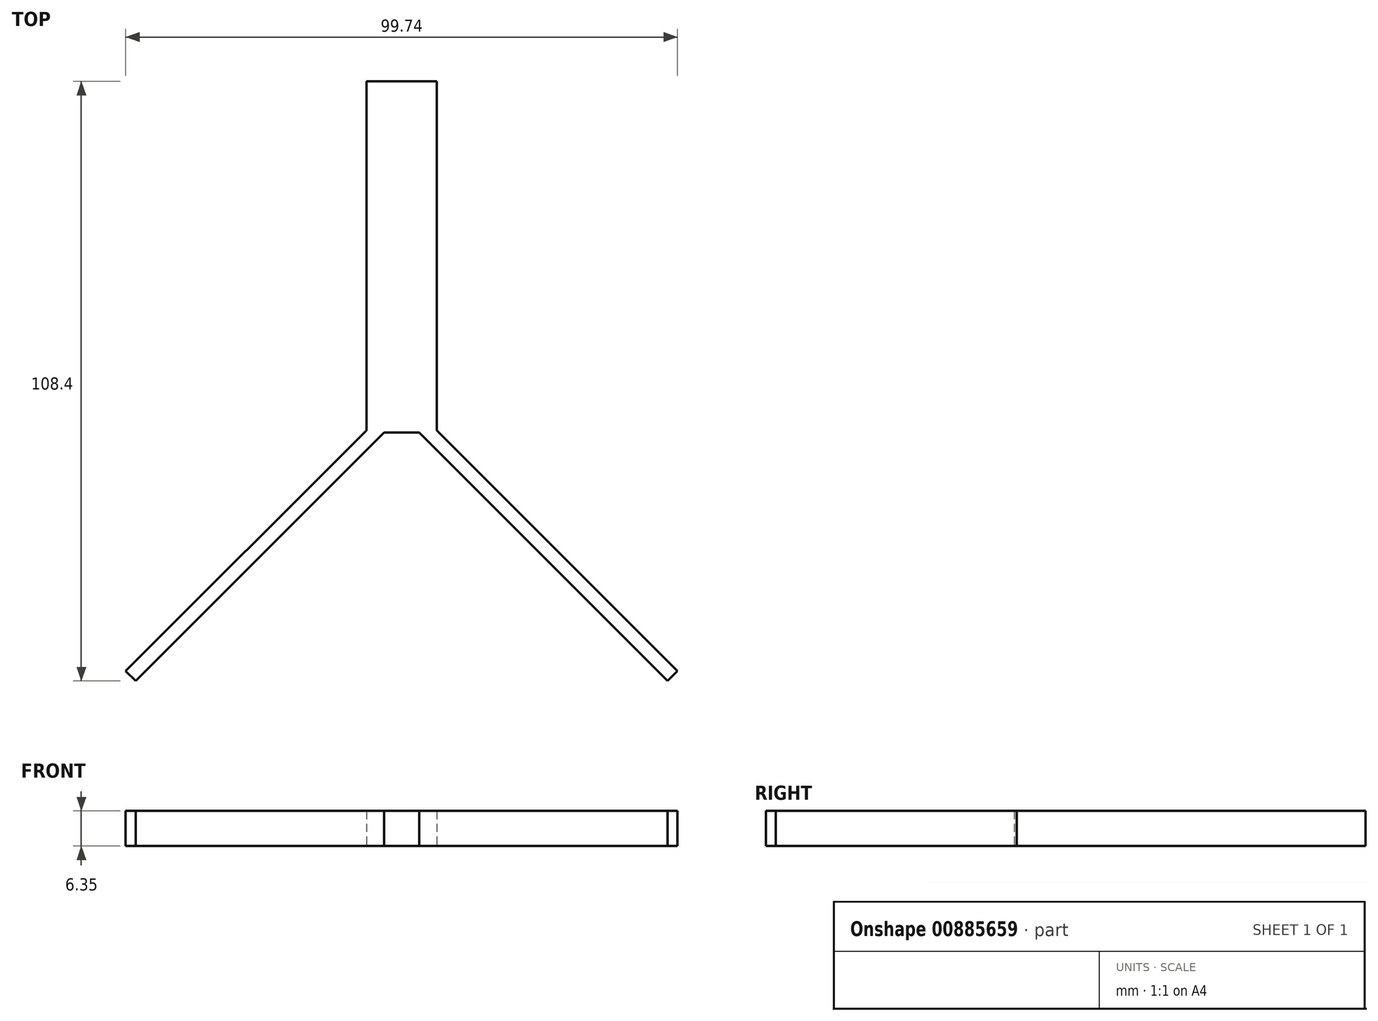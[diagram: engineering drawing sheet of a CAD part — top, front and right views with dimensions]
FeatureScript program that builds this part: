
annotation { "Feature Type Name" : "Feature", "Feature Type Description" : "" }
export const myFeature = defineFeature(function(context is Context, id is Id, definition is map)
    precondition{}
    {
        {
            var Q0;
            Q0=qCreatedBy(makeId("Top.planeOp"),FACE);
            var sketch = newSketch(context, id + "F0", { "sketchPlane" : qUnion([Q0])});
            skLineSegment(sketch, "E0.bottom", {"start": v(0, 0) * mm, "end": v(-6.35, 0) * mm});
            skLineSegment(sketch, "E0.top", {"start": v(0, -63.5) * mm, "end": v(-6.35, -63.5) * mm});
            skLineSegment(sketch, "E0.left", {"start": v(0, 0) * mm, "end": v(0, -63.5) * mm});
            skLineSegment(sketch, "E0.right", {"start": v(-6.35, 0) * mm, "end": v(-6.35, -63.5) * mm});
            skSolve(sketch);
        }
        {
            var Q0;
            Q0=makeQuery(id+"F0.imprint","IMPRINT",FACE,{"disambiguationData":[TD([[makeQuery(id+"F0.imprint","IMPRINT",EDGE,{"derivedFrom":sQuery(id+"F0.wireOp",EDGE,"E0.bottom")}),1.0]])]});
            var Q1;
            Q1=makeQuery(id+"F0.imprint","IMPRINT",FACE,{"disambiguationData":[TD([[makeQuery(id+"F0.imprint","IMPRINT",EDGE,{"derivedFrom":sQuery(id+"F0.wireOp",EDGE,"0yXSu1H6-dUJI-qaoZ-pFtF-Go9e8x1WTHV8.bottom")}),1.0]])]});
            extrude(context, id + "F1", {"entities" : qUnion([Q0, Q1]), "depth" : 6.35 * mm, "offsetDistance" : 25.4 * mm});
        }
        {
            var Q0;
            Q0=makeQuery(id+"F1.opExtrude","CAP_FACE",FACE,{"disambiguationData":[OSD([sQuery(id+"F0.wireOp",EDGE,"E0.bottom"),sQuery(id+"F0.wireOp",EDGE,"E0.top"),sQuery(id+"F0.wireOp",EDGE,"E0.left"),sQuery(id+"F0.wireOp",EDGE,"E0.right")])],"isStart":true});
            var sketch = newSketch(context, id + "F2", { "sketchPlane" : qUnion([Q0])});
            skLineSegment(sketch, "E1.bottom", {"start": v(-3.17, 63.5) * mm, "end": v(-4.97, 61.7) * mm});
            skLineSegment(sketch, "E1.top", {"start": v(-48.08, 108.4) * mm, "end": v(-49.87, 106.6) * mm});
            skLineSegment(sketch, "E1.left", {"start": v(-3.17, 63.5) * mm, "end": v(-48.08, 108.4) * mm});
            skLineSegment(sketch, "E1.right", {"start": v(-4.97, 61.7) * mm, "end": v(-49.87, 106.6) * mm});
            skSolve(sketch);
        }
        {
            var Q0;
            Q0 = qSketchRegion(id + "F2", true);
            extrude(context, id + "F3", {"entities" : qUnion([Q0]), "operationType" : NewBodyOperationType.ADD, "oppositeDirection" : true, "depth" : 6.35 * mm, "offsetDistance" : 25.4 * mm});
        }
        {
            var Q0;
            Q0=makeQuery(id+"F1.opExtrude","SWEPT_BODY",BODY,{"disambiguationData":[OSD([sQuery(id+"F0.wireOp",EDGE,"0yXSu1H6-dUJI-qaoZ-pFtF-Go9e8x1WTHV8.bottom"),sQuery(id+"F0.wireOp",EDGE,"0yXSu1H6-dUJI-qaoZ-pFtF-Go9e8x1WTHV8.top"),sQuery(id+"F0.wireOp",EDGE,"0yXSu1H6-dUJI-qaoZ-pFtF-Go9e8x1WTHV8.left"),sQuery(id+"F0.wireOp",EDGE,"0yXSu1H6-dUJI-qaoZ-pFtF-Go9e8x1WTHV8.right")])]});
            var Q1;
            Q1=makeQuery(id+"F1.opExtrude","SWEPT_BODY",BODY,{"disambiguationData":[OSD([sQuery(id+"F0.wireOp",EDGE,"E0.bottom"),sQuery(id+"F0.wireOp",EDGE,"E0.top"),sQuery(id+"F0.wireOp",EDGE,"E0.left"),sQuery(id+"F0.wireOp",EDGE,"E0.right")])]});
            var Q2;
            Q2=qCreatedBy(makeId("Right.planeOp"),FACE);
            mirror(context, id + "F4", {"operationType" : NewBodyOperationType.ADD, "entities" : qUnion([Q0, Q1]), "mirrorPlane" : qUnion([Q2])});
        }
    });
